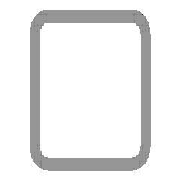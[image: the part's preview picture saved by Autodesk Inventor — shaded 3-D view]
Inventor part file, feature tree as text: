
AUTODESK INVENTOR PART (.ipt)
format: ipt  version: 2025 (Build 290162010, 162A)  size: 133,120 bytes
history: native  units: mm (DEFAULTED — no unit token found)
features: other x4, sketch x1, plane x1
ambient origin geometry x8: Origin, YZ Plane, XZ Plane, XY Plane, X Axis, Y Axis, Z Axis, Center Point
bodies: Solid1 (feature_tree), Body (feature_tree)
feature tree (6):
  parser-record x1  (decoder bookkeeping rows leaked as tree rows — omitted from the tree; the rows remain in map.json)
  other  "Driven Length"
  other  "Start Plane"
  other  "End Plane"
  sketch  "Sketch3"  dims[d3=2290.0mm d4=0.0mm d7=6.0mm d9=80.0mm d11=80.0mm d12=3.0mm d13=80.0mm d14=2370.0mm d15=40.0mm d16=40.0mm d17=90.0deg d18=2290.0mm]
  plane  "Work Plane3"
